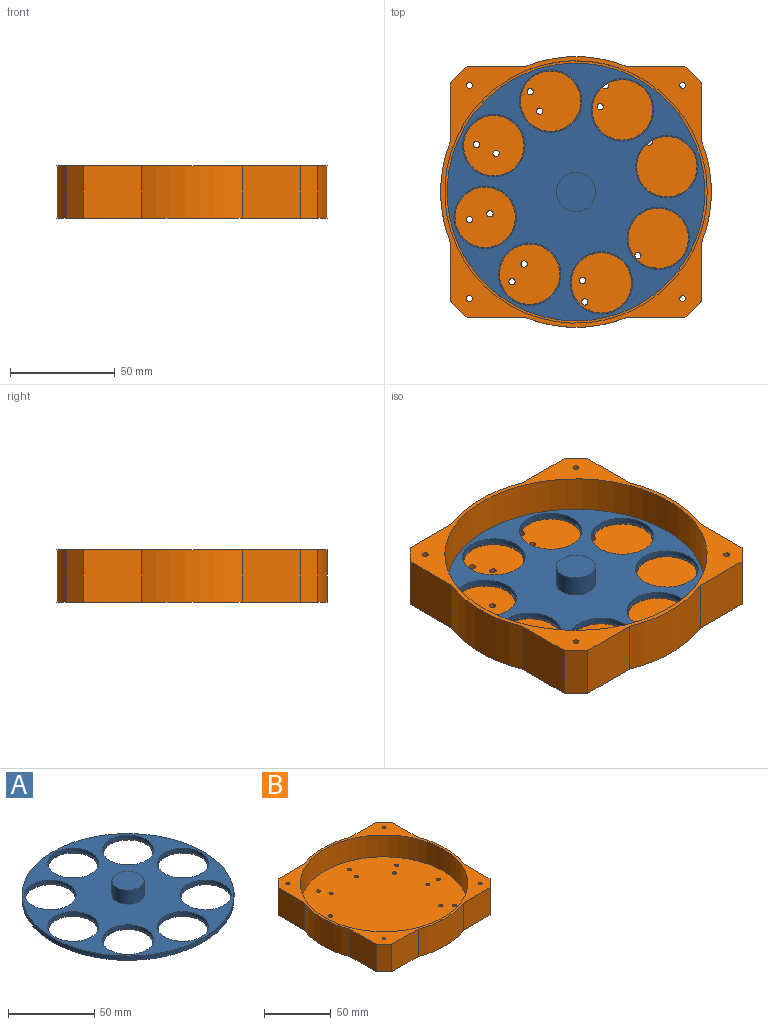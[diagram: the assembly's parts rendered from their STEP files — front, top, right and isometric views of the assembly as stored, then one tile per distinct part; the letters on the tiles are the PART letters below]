
ASSEMBLY  parts=2 mates=1
PART A: 29 faces, bbox 123x123x13 mm
  f0: cylinder r=61.5mm len=123mm, axis (0,0,-1), area 1174.7mm2, adj f9,f10
  f1: cylinder r=14.9mm len=29.8mm, axis (0,0,-1), area 237.8mm2, adj f9,f28
  f2: cylinder r=14.9mm len=29.8mm, axis (0,0,-1), area 237.8mm2, adj f9,f26
  f3: cylinder r=14.9mm len=29.8mm, axis (0,0,-1), area 237.8mm2, adj f9,f24
  f4: cylinder r=14.9mm len=29.8mm, axis (0,0,-1), area 237.8mm2, adj f9,f22
  f5: cylinder r=14.9mm len=29.8mm, axis (0,0,-1), area 237.8mm2, adj f9,f20
  f6: cylinder r=14.9mm len=29.8mm, axis (0,0,-1), area 237.8mm2, adj f9,f18
  f7: cylinder r=14.9mm len=29.8mm, axis (0,0,-1), area 237.8mm2, adj f9,f16
  f8: cylinder r=14.9mm len=29.8mm, axis (0,0,-1), area 237.8mm2, adj f9,f14
  f9: plane 123x123mm, normal (0,0,1), area 6027.9mm2, adj f0,f1,f2,f3,f4,f5,f6,f7
  f10: plane 123x123mm, normal (0,0,-1), area 6670.8mm2, adj f0,f13,f15,f17,f19,f21,f23,f25
  f11: cylinder r=9.35mm len=18.7mm, axis (0,0,-1), area 585.1mm2, adj f9,f12
  f12: plane 18.7x18.7mm, normal (0,0,1), area 274.6mm2, adj f11
  f13: cylinder r=14.4mm len=28.8mm, axis (0,0,-1), area 45.2mm2, adj f10,f14
  f14: plane 29.8x29.8mm, normal (0,0,1), area 46mm2, adj f8,f13
  f15: cylinder r=14.4mm len=28.8mm, axis (0,0,-1), area 45.2mm2, adj f10,f16
  f16: plane 29.8x29.8mm, normal (0,0,1), area 46mm2, adj f7,f15
  f17: cylinder r=14.4mm len=28.8mm, axis (0,0,-1), area 45.2mm2, adj f10,f18
  f18: plane 29.8x29.8mm, normal (0,0,1), area 46mm2, adj f6,f17
  f19: cylinder r=14.4mm len=28.8mm, axis (0,0,-1), area 45.2mm2, adj f10,f20
  f20: plane 29.8x29.8mm, normal (0,0,1), area 46mm2, adj f5,f19
  f21: cylinder r=14.4mm len=28.8mm, axis (0,0,-1), area 45.2mm2, adj f10,f22
  f22: plane 29.8x29.8mm, normal (0,0,1), area 46mm2, adj f4,f21
  f23: cylinder r=14.4mm len=28.8mm, axis (0,0,-1), area 45.2mm2, adj f10,f24
  f24: plane 29.8x29.8mm, normal (0,0,1), area 46mm2, adj f3,f23
  f25: cylinder r=14.4mm len=28.8mm, axis (0,0,-1), area 45.2mm2, adj f10,f26
  f26: plane 29.8x29.8mm, normal (0,0,1), area 46mm2, adj f2,f25
  f27: cylinder r=14.4mm len=28.8mm, axis (0,0,-1), area 45.2mm2, adj f10,f28
  f28: plane 29.8x29.8mm, normal (0,0,1), area 46mm2, adj f1,f27
PART B: 60 faces, bbox 129.2x129.2x25 mm
  f0: cylinder r=1.5mm len=3mm, axis (0,0,-1), area 28.3mm2, adj f18,f46
  f1: cylinder r=1.5mm len=3mm, axis (0,0,-1), area 28.3mm2, adj f18,f49
  f2: cylinder r=1.5mm len=3mm, axis (0,0,-1), area 28.3mm2, adj f18,f48
  f3: cylinder r=1.5mm len=3mm, axis (0,0,-1), area 28.3mm2, adj f18,f51
  f4: cylinder r=1.5mm len=3mm, axis (0,0,-1), area 28.3mm2, adj f18,f50
  f5: cylinder r=1.5mm len=3mm, axis (0,0,-1), area 28.3mm2, adj f18,f59
  f6: cylinder r=1.5mm len=3mm, axis (0,0,-1), area 28.3mm2, adj f18,f58
  f7: cylinder r=1.5mm len=3mm, axis (0,0,-1), area 28.3mm2, adj f18,f57
  f8: cylinder r=1.5mm len=3mm, axis (0,0,-1), area 28.3mm2, adj f18,f56
  f9: cylinder r=1.5mm len=3mm, axis (0,0,-1), area 28.3mm2, adj f18,f55
  f10: cylinder r=1.5mm len=3mm, axis (0,0,-1), area 28.3mm2, adj f18,f54
  f11: cylinder r=1.5mm len=3mm, axis (0,0,-1), area 28.3mm2, adj f18,f53
  f12: cylinder r=1.5mm len=3mm, axis (0,0,-1), area 28.3mm2, adj f18,f52
  f13: cylinder r=1.5mm len=3mm, axis (0,0,-1), area 28.3mm2, adj f18,f43
  f14: cylinder r=1.5mm len=3mm, axis (0,0,-1), area 28.3mm2, adj f18,f42
  f15: cylinder r=1.5mm len=3mm, axis (0,0,-1), area 28.3mm2, adj f18,f45
  f16: cylinder r=1.5mm len=3mm, axis (0,0,-1), area 28.3mm2, adj f18,f44
  f17: cylinder r=1.5mm len=3mm, axis (0,0,-1), area 28.3mm2, adj f18,f47
  f18: plane 125.19x125.19mm, normal (0,0,1), area 12181.9mm2, adj f0,f1,f2,f3,f4,f5,f6,f7
  f19: plane 129.19x129.19mm, normal (0,0,-1), area 14145.3mm2, adj f20,f21,f22,f23,f24,f25,f26,f27
  f20: plane 28.07x25mm, normal (-1,0,0), area 701.8mm2, adj f19,f21,f38,f41
  f21: cylinder r=64.59mm len=47.85mm, axis (0,0,-1), area 1225.6mm2, adj f19,f20,f22,f41
  f22: plane 28.07x25mm, normal (-1,0,0), area 701.8mm2, adj f19,f21,f23,f41
  f23: plane 25x8mm, normal (-0.71,-0.71,0), area 282.8mm2, adj f19,f22,f24,f41
  f24: plane 28.07x25mm, normal (0,-1,0), area 701.8mm2, adj f19,f23,f25,f41
  f25: cylinder r=64.59mm len=47.85mm, axis (0,0,-1), area 1225.6mm2, adj f19,f24,f26,f41
  f26: plane 28.07x25mm, normal (0,-1,0), area 701.8mm2, adj f19,f25,f27,f41
  f27: plane 25x8mm, normal (0.71,-0.71,0), area 282.8mm2, adj f19,f26,f28,f41
  f28: plane 28.07x25mm, normal (1,0,0), area 701.8mm2, adj f19,f27,f29,f41
  f29: cylinder r=64.59mm len=47.85mm, axis (0,0,-1), area 1225.6mm2, adj f19,f28,f30,f41
  f30: plane 28.07x25mm, normal (1,0,0), area 701.8mm2, adj f19,f29,f31,f41
  f31: plane 25x8mm, normal (0.71,0.71,0), area 282.8mm2, adj f19,f30,f32,f41
  f32: plane 28.07x25mm, normal (0,1,0), area 701.8mm2, adj f19,f31,f33,f41
  f33: cylinder r=64.59mm len=47.85mm, axis (0,0,-1), area 1225.6mm2, adj f19,f32,f34,f41
  f34: plane 28.07x25mm, normal (0,1,0), area 701.8mm2, adj f19,f33,f38,f41
  f35: cylinder r=1.4mm len=25mm, axis (0,0,-1), area 219.9mm2, adj f19,f41
  f36: cylinder r=1.4mm len=25mm, axis (0,0,-1), area 219.9mm2, adj f19,f41
  f37: cylinder r=1.4mm len=25mm, axis (0,0,-1), area 219.9mm2, adj f19,f41
  f38: plane 25x8mm, normal (-0.71,0.71,0), area 282.8mm2, adj f19,f20,f34,f41
  f39: cylinder r=62.59mm len=125.19mm, axis (0,0,-1), area 7865.9mm2, adj f18,f41
  f40: cylinder r=1.4mm len=25mm, axis (0,0,-1), area 219.9mm2, adj f19,f41
  f41: plane 129.19x129.19mm, normal (0,0,1), area 2528.9mm2, adj f20,f21,f22,f23,f24,f25,f26,f27
  f42: torus R=3.5mm, axis (0,0,1), area 44mm2, adj f14,f19
  f43: torus R=3.5mm, axis (0,0,1), area 44mm2, adj f13,f19
  f44: torus R=3.5mm, axis (0,0,1), area 44mm2, adj f16,f19
  f45: torus R=3.5mm, axis (0,0,1), area 44mm2, adj f15,f19
  f46: torus R=3.5mm, axis (0,0,1), area 44mm2, adj f0,f19
  f47: torus R=3.5mm, axis (0,0,1), area 44mm2, adj f17,f19
  f48: torus R=3.5mm, axis (0,0,1), area 44mm2, adj f2,f19
  f49: torus R=3.5mm, axis (0,0,1), area 44mm2, adj f1,f19
  f50: torus R=3.5mm, axis (0,0,1), area 44mm2, adj f4,f19
  f51: torus R=3.5mm, axis (0,0,1), area 44mm2, adj f3,f19
  f52: torus R=3.5mm, axis (0,0,1), area 44mm2, adj f12,f19
  f53: torus R=3.5mm, axis (0,0,1), area 44mm2, adj f11,f19
  f54: torus R=3.5mm, axis (0,0,1), area 44mm2, adj f10,f19
  f55: torus R=3.5mm, axis (0,0,1), area 44mm2, adj f9,f19
  f56: torus R=3.5mm, axis (0,0,1), area 44mm2, adj f8,f19
  f57: torus R=3.5mm, axis (0,0,1), area 44mm2, adj f7,f19
  f58: torus R=3.5mm, axis (0,0,1), area 44mm2, adj f6,f19
  f59: torus R=3.5mm, axis (0,0,1), area 44mm2, adj f5,f19
PLACE A rot(axis=(0,0,1),15.6deg) t=(25.57,158.82,22.36)mm
PLACE B t=(25.57,158.82,17.36)mm fixed
MATE revolute B.f39 <-> A.f0  axis (0,0,1) through (25.57,158.82,22.36)mm
